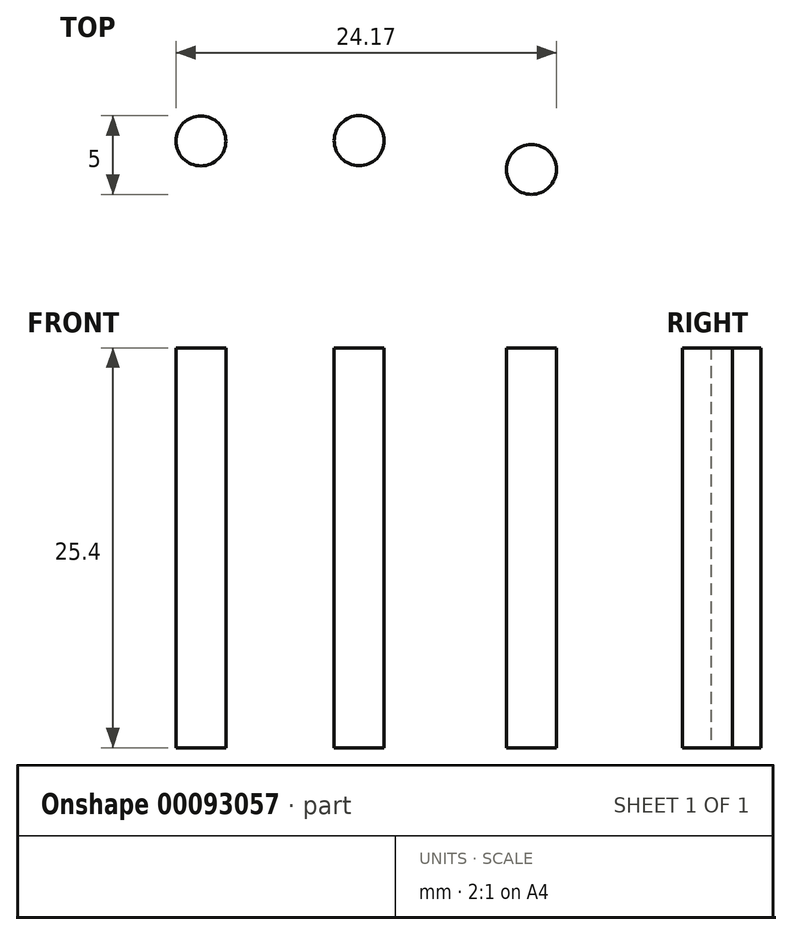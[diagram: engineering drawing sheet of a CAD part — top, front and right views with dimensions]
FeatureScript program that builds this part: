
annotation { "Feature Type Name" : "Feature", "Feature Type Description" : "" }
export const myFeature = defineFeature(function(context is Context, id is Id, definition is map)
    precondition{}
    {
        {
            var Q0;
            Q0=qCreatedBy(makeId("Top.planeOp"),FACE);
            var sketch = newSketch(context, id + "F0", { "sketchPlane" : qUnion([Q0])});
            skCircle(sketch, "E0", {"center": v(-54.48, 10.7) * mm, "radius": 1.59 * mm});
            skCircle(sketch, "E1", {"center": v(-44.43, 10.71) * mm, "radius": 1.59 * mm});
            skCircle(sketch, "E2", {"center": v(-33.49, 8.89) * mm, "radius": 1.59 * mm});
            skSolve(sketch);
        }
        {
            var Q0;
            Q0=makeQuery(id+"F0.imprint","IMPRINT",FACE,{"disambiguationData":[TD([[makeQuery(id+"F0.imprint","IMPRINT",EDGE,{"derivedFrom":sQuery(id+"F0.wireOp",EDGE,"E0")}),1.0]])]});
            var Q1;
            Q1=makeQuery(id+"F0.imprint","IMPRINT",FACE,{"disambiguationData":[TD([[makeQuery(id+"F0.imprint","IMPRINT",EDGE,{"derivedFrom":sQuery(id+"F0.wireOp",EDGE,"E1")}),1.0]])]});
            var Q2;
            Q2=makeQuery(id+"F0.imprint","IMPRINT",FACE,{"disambiguationData":[TD([[makeQuery(id+"F0.imprint","IMPRINT",EDGE,{"derivedFrom":sQuery(id+"F0.wireOp",EDGE,"E2")}),1.0]])]});
            var Q3;
            Q3=sQuery(id+"F0.wireOp",EDGE,"E0");
            extrude(context, id + "F1", {"entities" : qUnion([Q0, Q1, Q2]), "surfaceEntities" : qUnion([Q3]), "depth" : 25.4 * mm});
        }
    });
